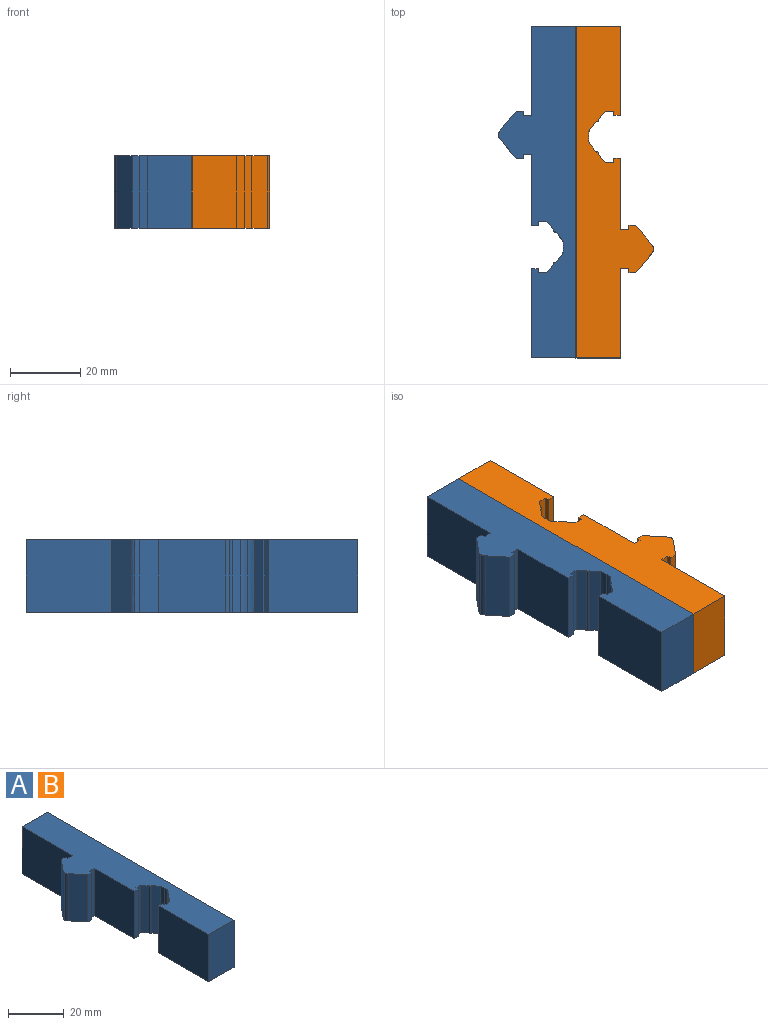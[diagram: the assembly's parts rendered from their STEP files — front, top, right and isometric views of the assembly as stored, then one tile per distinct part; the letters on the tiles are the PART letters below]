
ASSEMBLY  parts=2 mates=1
PART A: 32 faces, bbox 22.1x94.5x20.6 mm
  f0: plane 20.64x5.39mm, normal (-0.77,0.64,0), area 144.2mm2, adj f1,f29,f30,f31
  f1: extruded ~20.64x1.36mm, area 31mm2, adj f0,f2,f30,f31
  f2: extruded ~20.64x1.36mm, area 31mm2, adj f1,f3,f30,f31
  f3: plane 20.64x5.39mm, normal (-0.77,-0.64,0), area 144.2mm2, adj f2,f4,f30,f31
  f4: plane 20.64x1.98mm, normal (0,-1,0), area 41mm2, adj f3,f5,f30,f31
  f5: plane 20.64x1.19mm, normal (1,0,0), area 24.6mm2, adj f4,f6,f30,f31
  f6: plane 20.64x2.38mm, normal (0,-1,0), area 49.1mm2, adj f5,f7,f30,f31
  f7: plane 20.64x20.24mm, normal (-1,0,0), area 417.8mm2, adj f6,f8,f30,f31
  f8: plane 20.64x1.98mm, normal (0,-1,0), area 41mm2, adj f7,f9,f30,f31
  f9: plane 20.64x1.19mm, normal (1,0,0), area 24.6mm2, adj f8,f10,f30,f31
  f10: plane 20.64x2.38mm, normal (0,-1,0), area 49.1mm2, adj f9,f11,f30,f31
  f11: plane 20.64x2.37mm, normal (-0.77,-0.64,0), area 63.9mm2, adj f10,f12,f30,f31
  f12: cylinder r=0.4mm len=20.64mm, axis (0,0,-1), area 25.7mm2, adj f11,f13,f30,f31
  f13: plane 20.64x2.37mm, normal (-0.77,-0.64,0), area 63.9mm2, adj f12,f14,f30,f31
  f14: extruded ~20.64x1.99mm, area 41.7mm2, adj f13,f15,f30,f31
  f15: extruded ~20.64x1.99mm, area 41.7mm2, adj f14,f16,f30,f31
  f16: plane 20.64x2.37mm, normal (-0.77,0.64,0), area 63.9mm2, adj f15,f17,f30,f31
  f17: cylinder r=0.4mm len=20.64mm, axis (0,0,-1), area 25.7mm2, adj f16,f18,f30,f31
  f18: plane 20.64x2.37mm, normal (-0.77,0.64,0), area 63.9mm2, adj f17,f19,f30,f31
  f19: plane 20.64x2.38mm, normal (0,1,0), area 49.1mm2, adj f18,f20,f30,f31
  f20: plane 20.64x1.19mm, normal (1,0,0), area 24.6mm2, adj f19,f21,f30,f31
  f21: plane 20.64x1.98mm, normal (0,1,0), area 41mm2, adj f20,f22,f30,f31
  f22: plane 25.4x20.64mm, normal (-1,0,0), area 524.2mm2, adj f21,f23,f30,f31
  f23: plane 20.64x12.7mm, normal (0,-1,0), area 262.1mm2, adj f22,f24,f30,f31
  f24: plane 94.46x20.64mm, normal (1,0,0), area 1949.4mm2, adj f23,f25,f30,f31
  f25: plane 20.64x12.7mm, normal (0,1,0), area 262.1mm2, adj f24,f26,f30,f31
  f26: plane 25.4x20.64mm, normal (-1,0,0), area 524.2mm2, adj f25,f27,f30,f31
  f27: plane 20.64x2.38mm, normal (0,1,0), area 49.1mm2, adj f26,f28,f30,f31
  f28: plane 20.64x1.19mm, normal (1,0,0), area 24.6mm2, adj f27,f29,f30,f31
  f29: plane 20.64x1.98mm, normal (0,1,0), area 41mm2, adj f0,f28,f30,f31
  f30: plane 94.46x22.11mm, normal (0,0,1), area 1188.3mm2, adj f0,f1,f2,f3,f4,f5,f6,f7
  f31: plane 94.46x22.11mm, normal (0,0,-1), area 1188.3mm2, adj f0,f1,f2,f3,f4,f5,f6,f7
PART B: same geometry as A
PLACE A t=(1.08,-6.61,8.11)mm
PLACE B rot(axis=(0,0,1),180deg) t=(-91.05,-41.47,8.11)mm
MATE planar B.f24 <-> A.f24  axis (-1,0,0) through (-44.98,-24.04,18.42)mm
